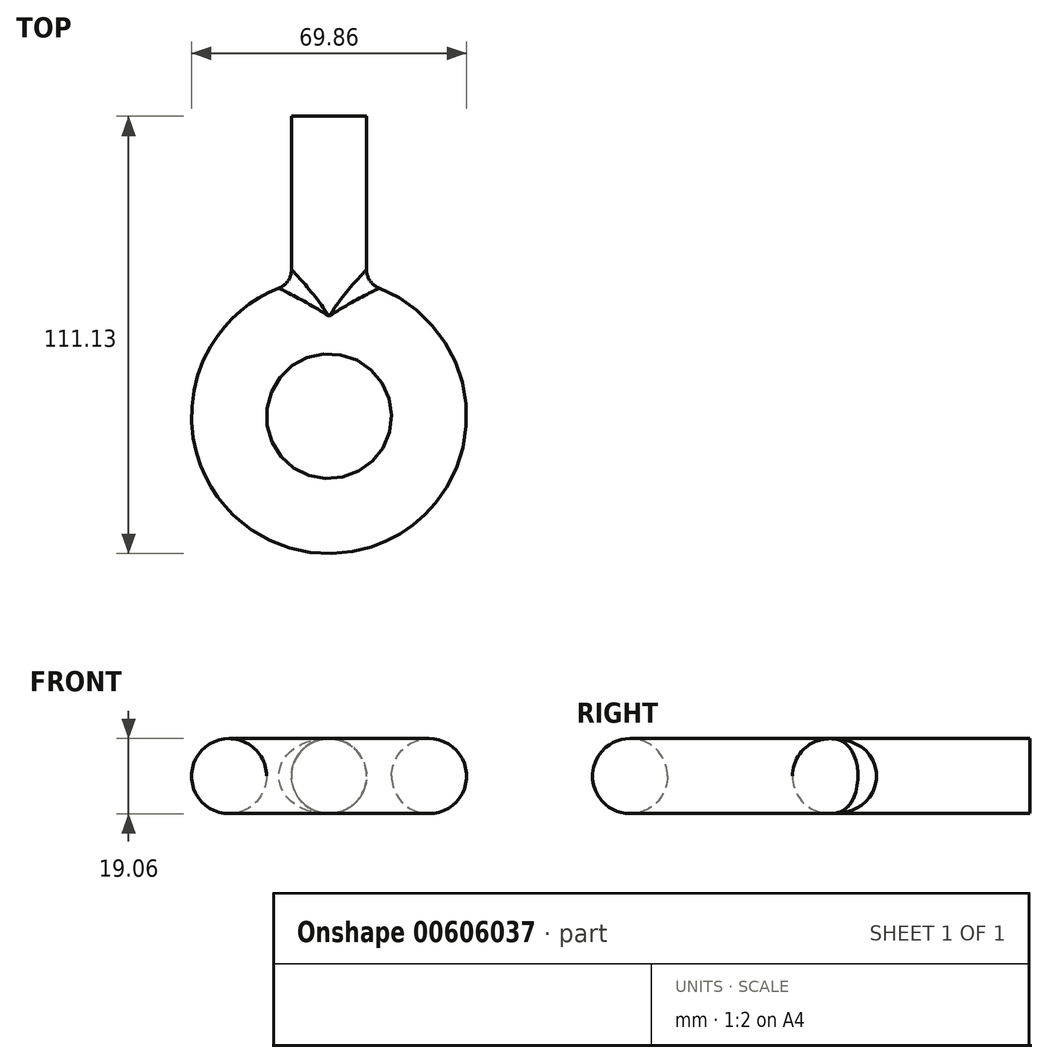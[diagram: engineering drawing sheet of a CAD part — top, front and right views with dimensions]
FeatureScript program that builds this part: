
annotation { "Feature Type Name" : "Feature", "Feature Type Description" : "" }
export const myFeature = defineFeature(function(context is Context, id is Id, definition is map)
    precondition{}
    {
        {
            var Q0;
            Q0=qCreatedBy(makeId("Front.planeOp"),FACE);
            var sketch = newSketch(context, id + "F0", { "sketchPlane" : qUnion([Q0])});
            skCircle(sketch, "E0", {"center": v(0, 0) * mm, "radius": 9.53 * mm});
            skSolve(sketch);
        }
        {
            var Q0;
            Q0 = qSketchRegion(id + "F0", true);
            extrude(context, id + "F1", {"entities" : qUnion([Q0]), "depth" : 50.8 * mm, "offsetDistance" : 25.4 * mm});
        }
        {
            var Q0;
            Q0=makeQuery(id+"F1.opExtrude","CAP_FACE",FACE,{"disambiguationData":[OSD([sQuery(id+"F0.wireOp",EDGE,"E0")])],"isStart":false});
            var sketch = newSketch(context, id + "F2", { "sketchPlane" : qUnion([Q0])});
            skLineSegment(sketch, "E1", {"start": v(0, 9.53) * mm, "end": v(0, -9.53) * mm});
            skSolve(sketch);
        }
        {
            var Q0;
            {var subQ0=sQuery(id+"F2.wireOp",EDGE,"E1");Q0=makeQuery(id+"F2.imprint","IMPRINT",FACE,{"disambiguationData":[TD([[makeQuery(id+"F2.imprint","IMPRINT",EDGE,{"derivedFrom":subQ0}),1.0]])]});}
            var Q1;
            Q1=sQuery(id+"F2.wireOp",EDGE,"E1");
            revolve(context, id + "F3", {"operationType" : NewBodyOperationType.ADD, "entities" : qUnion([Q0]), "axis" : qUnion([Q1]), "revolveType" : RevolveType.FULL});
        }
        {
            var Q0;
            Q0=qCreatedBy(makeId("Top.planeOp"),FACE);
            var sketch = newSketch(context, id + "F4", { "sketchPlane" : qUnion([Q0])});
            skCircle(sketch, "E2", {"center": v(0, -76.2) * mm, "radius": 25.4 * mm});
            skSolve(sketch);
        }
        {
            var Q0;
            Q0=qCreatedBy(makeId("Right.planeOp"),FACE);
            var sketch = newSketch(context, id + "F5", { "sketchPlane" : qUnion([Q0])});
            skCircle(sketch, "E3", {"center": v(-50.8, 0) * mm, "radius": 9.53 * mm});
            skSolve(sketch);
        }
        {
            var Q0;
            Q0=makeQuery(id+"F5.imprint","IMPRINT",FACE,{"disambiguationData":[TD([[makeQuery(id+"F5.imprint","IMPRINT",EDGE,{"derivedFrom":sQuery(id+"F5.wireOp",EDGE,"E3")}),1.0]])]});
            var Q1;
            Q1=sQuery(id+"F4.wireOp",EDGE,"E2");
            sweep(context, id + "F6", {"operationType" : NewBodyOperationType.ADD, "profiles" : qUnion([Q0]), "path" : qUnion([Q1])});
        }
        {
            var Q0;
            Q0=makeQuery(id+"F6.boolean.opBoolean","INTERSECT",EDGE,{"disambiguationData":[OD(0.0)],"derivedFrom":[makeQuery(id+"F1.opExtrude","SWEPT_FACE",FACE,{"disambiguationData":[OSD([sQuery(id+"F0.wireOp",EDGE,"E0")])]}),makeQuery(id+"F6.opSweep","SWEPT_FACE",FACE,{"disambiguationData":[OSD([sQuery(id+"F4.wireOp",EDGE,"E2"),sQuery(id+"F5.wireOp",EDGE,"E3")])]})]});
            var Q1;
            Q1=makeQuery(id+"F6.boolean.opBoolean","INTERSECT",EDGE,{"disambiguationData":[OD(1.0)],"derivedFrom":[makeQuery(id+"F1.opExtrude","SWEPT_FACE",FACE,{"disambiguationData":[OSD([sQuery(id+"F0.wireOp",EDGE,"E0")])]}),makeQuery(id+"F6.opSweep","SWEPT_FACE",FACE,{"disambiguationData":[OSD([sQuery(id+"F4.wireOp",EDGE,"E2"),sQuery(id+"F5.wireOp",EDGE,"E3")])]})]});
            fillet(context, id + "F7", {"entities" : qUnion([Q0, Q1]), "radius" : 5.08 * mm, "tangentPropagation" : true, "allowEdgeOverflow" : false});
        }
    });
